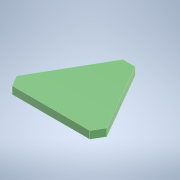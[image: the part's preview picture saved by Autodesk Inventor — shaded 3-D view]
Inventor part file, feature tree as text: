
AUTODESK INVENTOR PART (.ipt)
format: ipt  version: 2021 (Build 250183000, 183)  size: 116,736 bytes
history: native  units: mm
features: extrude x1, sketch x1
ambient origin geometry x8: Origin, YZ Plane, XZ Plane, XY Plane, X Axis, Y Axis, Z Axis, Center Point
bodies: Solid1 (feature_tree)
feature tree (2):
  extrude  "Extrusion1"  Depth=1.9mm
  sketch  "Sketch1"  dims[d0=19.6mm d1=3.117692mm d2=1.9mm d3=0.0mm d4=14.866667mm d5=22.3mm]
